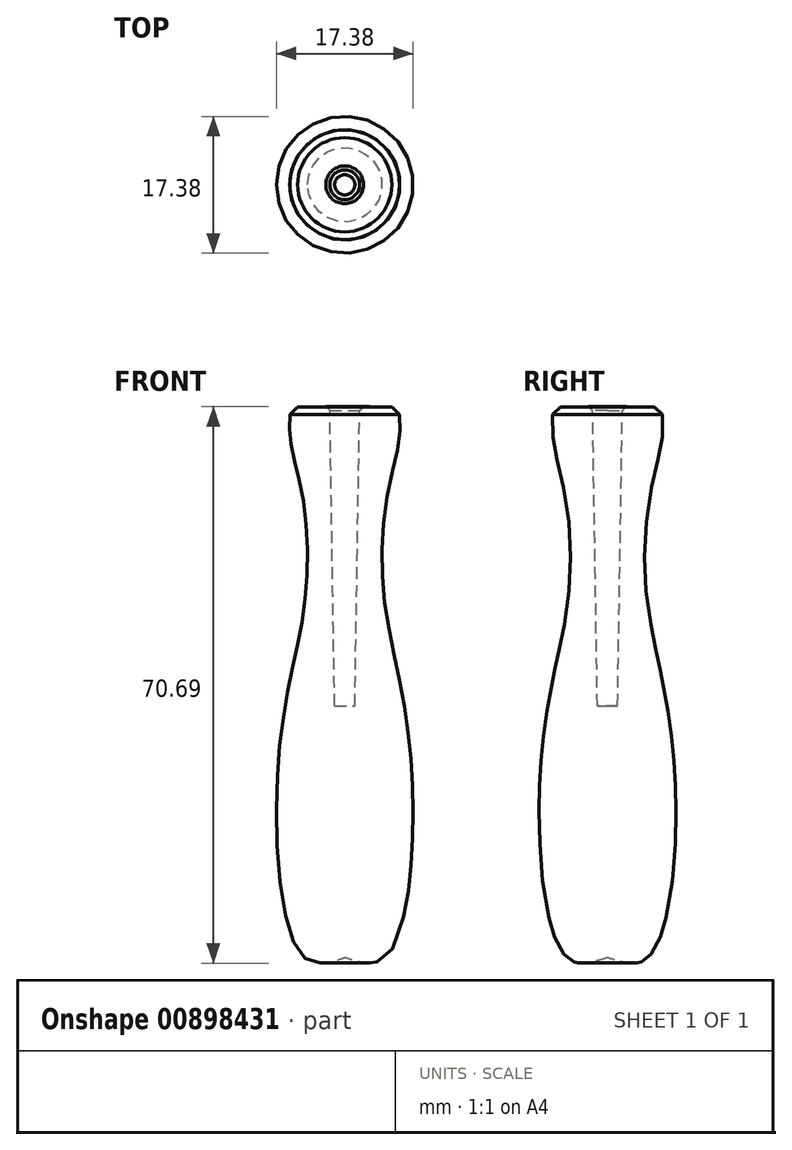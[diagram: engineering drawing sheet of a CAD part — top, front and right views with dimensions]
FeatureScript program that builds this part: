
annotation { "Feature Type Name" : "Feature", "Feature Type Description" : "" }
export const myFeature = defineFeature(function(context is Context, id is Id, definition is map)
    precondition{}
    {
        {
            var Q0;
            Q0=qCreatedBy(makeId("Front.planeOp"),FACE);
            var sketch = newSketch(context, id + "F0", { "sketchPlane" : qUnion([Q0])});
            skLineSegment(sketch, "E0", {"start": v(0, -38) * mm, "end": v(-1.28, -38) * mm});
            skLineSegment(sketch, "E1", {"start": v(-1.29, -38) * mm, "end": v(-1.9, 0) * mm});
            skLineSegment(sketch, "E2", {"start": v(0, -70) * mm, "end": v(0, -38) * mm});
            skLineSegment(sketch, "E3", {"start": v(0, 0) * mm, "end": v(-1.9, 0) * mm});
            skLineSegment(sketch, "E4", {"start": v(-1.9, 0) * mm, "end": v(-6.9, -0.08) * mm});
            skFitSpline(sketch, "E5", {"points": [v(-6.9, -0.08) * mm, v(-6.9, -4.34) * mm, v(-5.34, -11.46) * mm, v(-4.92, -23.6) * mm, v(-6.9, -34.48) * mm, v(-8.7, -51.44) * mm, v(-5.13, -70) * mm, v(0, -70) * mm], "startDerivative": vector(-3.31, -44.22) * mm, "endDerivative": vector(55.3, 17.82) * mm});
            skSolve(sketch);
        }
        {
            var Q0;
            Q0=makeQuery(id+"F0.imprint","IMPRINT",FACE,{"disambiguationData":[TD([[makeQuery(id+"F0.imprint","IMPRINT",EDGE,{"derivedFrom":sQuery(id+"F0.wireOp",EDGE,"E0")}),1.0]])]});
            var Q1;
            Q1=sQuery(id+"F0.wireOp",EDGE,"E2");
            revolve(context, id + "F1", {"surfaceOperationType" : NewSurfaceOperationType.NEW, "entities" : qUnion([Q0]), "axis" : qUnion([Q1]), "revolveType" : RevolveType.FULL});
        }
        {
            var Q0;
            Q0=makeQuery(id+"F1.opRevolve","SWEPT_EDGE",EDGE,{"disambiguationData":[OSD([sQuery(id+"F0.wireOp",EDGE,"E1"),sQuery(id+"F0.wireOp",EDGE,"E4")])]});
            chamfer(context, id + "F2", {"entities" : qUnion([Q0]), "width" : 0.5 * mm, "tangentPropagation" : true});
        }
        {
            var Q0;
            Q0=makeQuery(id+"F1.opRevolve","SWEPT_EDGE",EDGE,{"disambiguationData":[OSD([sQuery(id+"F0.wireOp",EDGE,"E4"),sQuery(id+"F0.wireOp",EDGE,"E5")])]});
            chamfer(context, id + "F3", {"entities" : qUnion([Q0]), "width" : 1 * mm, "tangentPropagation" : true});
        }
    });
